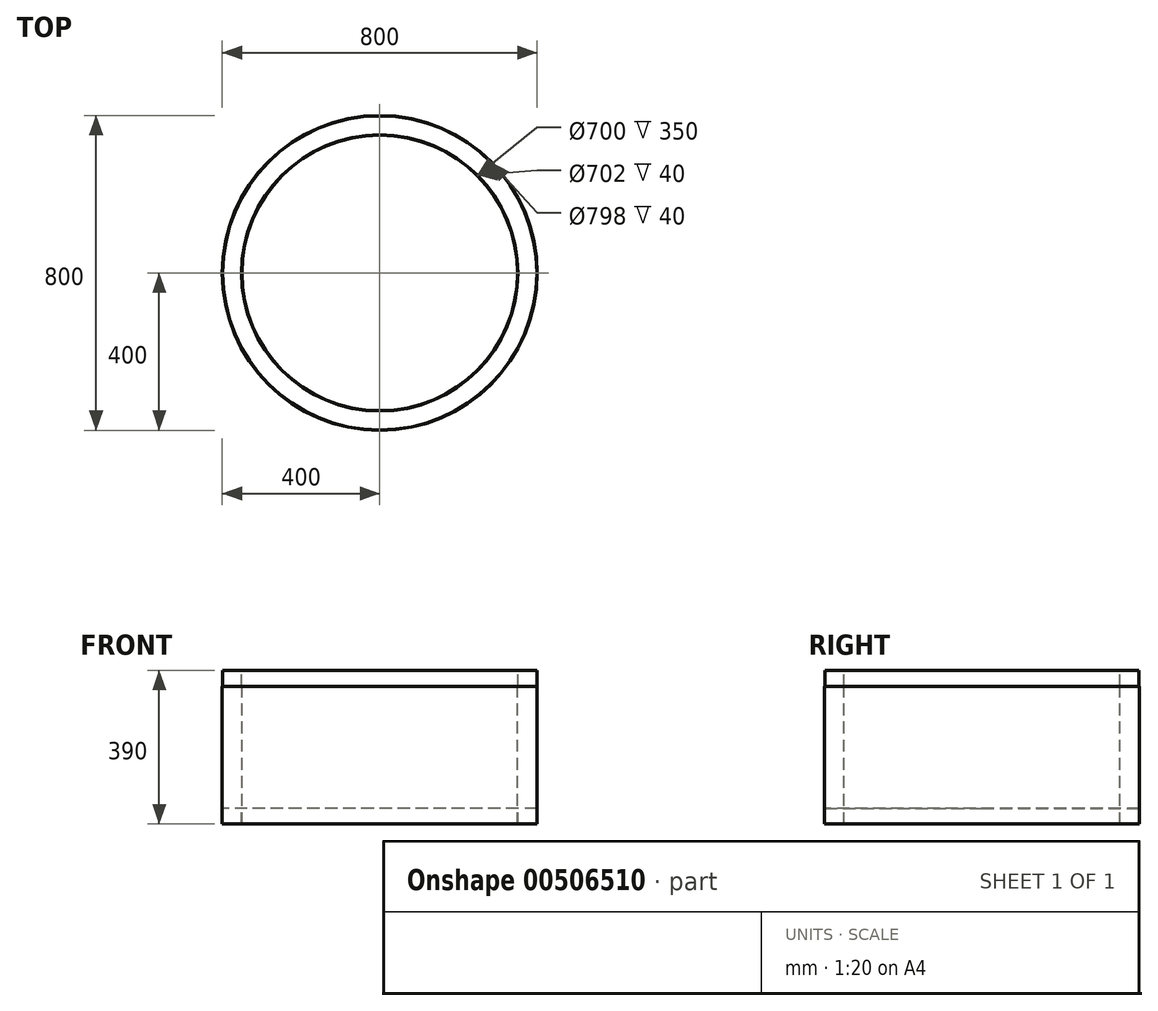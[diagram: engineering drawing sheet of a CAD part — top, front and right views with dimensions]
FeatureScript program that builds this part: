
annotation { "Feature Type Name" : "Feature", "Feature Type Description" : "" }
export const myFeature = defineFeature(function(context is Context, id is Id, definition is map)
    precondition{}
    {
        {
            var Q0;
            Q0=qCreatedBy(makeId("Front.planeOp"),FACE);
            var sketch = newSketch(context, id + "F0", { "sketchPlane" : qUnion([Q0])});
            skLineSegment(sketch, "E0", {"start": v(0, 74.87) * mm, "end": v(0, -73.71) * mm, "construction": true});
            skLineSegment(sketch, "E1", {"start": v(0, 374.84) * mm, "end": v(0, -528.94) * mm, "construction": true});
            skLineSegment(sketch, "E2", {"start": v(-350, -489.75) * mm, "end": v(-350, -139.75) * mm});
            skLineSegment(sketch, "E3", {"start": v(-350, -139.75) * mm, "end": v(-351, -139.75) * mm});
            skLineSegment(sketch, "E4", {"start": v(-351, -139.75) * mm, "end": v(-351, -99.75) * mm});
            skLineSegment(sketch, "E5", {"start": v(-351, -99.75) * mm, "end": v(-399, -99.75) * mm});
            skLineSegment(sketch, "E6", {"start": v(-399, -99.75) * mm, "end": v(-399, -139.75) * mm});
            skLineSegment(sketch, "E7", {"start": v(-399, -139.75) * mm, "end": v(-400, -139.75) * mm});
            skLineSegment(sketch, "E8", {"start": v(-400, -139.75) * mm, "end": v(-400, -489.75) * mm});
            skLineSegment(sketch, "E9", {"start": v(-400, -489.75) * mm, "end": v(-399, -489.75) * mm});
            skLineSegment(sketch, "E10", {"start": v(-399, -489.75) * mm, "end": v(-399, -449.75) * mm});
            skLineSegment(sketch, "E11", {"start": v(-399, -449.75) * mm, "end": v(-351, -449.75) * mm});
            skLineSegment(sketch, "E12", {"start": v(-351, -449.75) * mm, "end": v(-351, -489.75) * mm});
            skLineSegment(sketch, "E13", {"start": v(-351, -489.75) * mm, "end": v(-350, -489.75) * mm});
            skSolve(sketch);
        }
        {
            var Q0;
            Q0=qSketchRegion(id+"F0",true);
            var Q1;
            Q1=sQuery(id+"F0.wireOp",EDGE,"E1");
            revolve(context, id + "F1", {"entities" : qUnion([Q0]), "axis" : qUnion([Q1]), "revolveType" : RevolveType.FULL});
        }
    });
